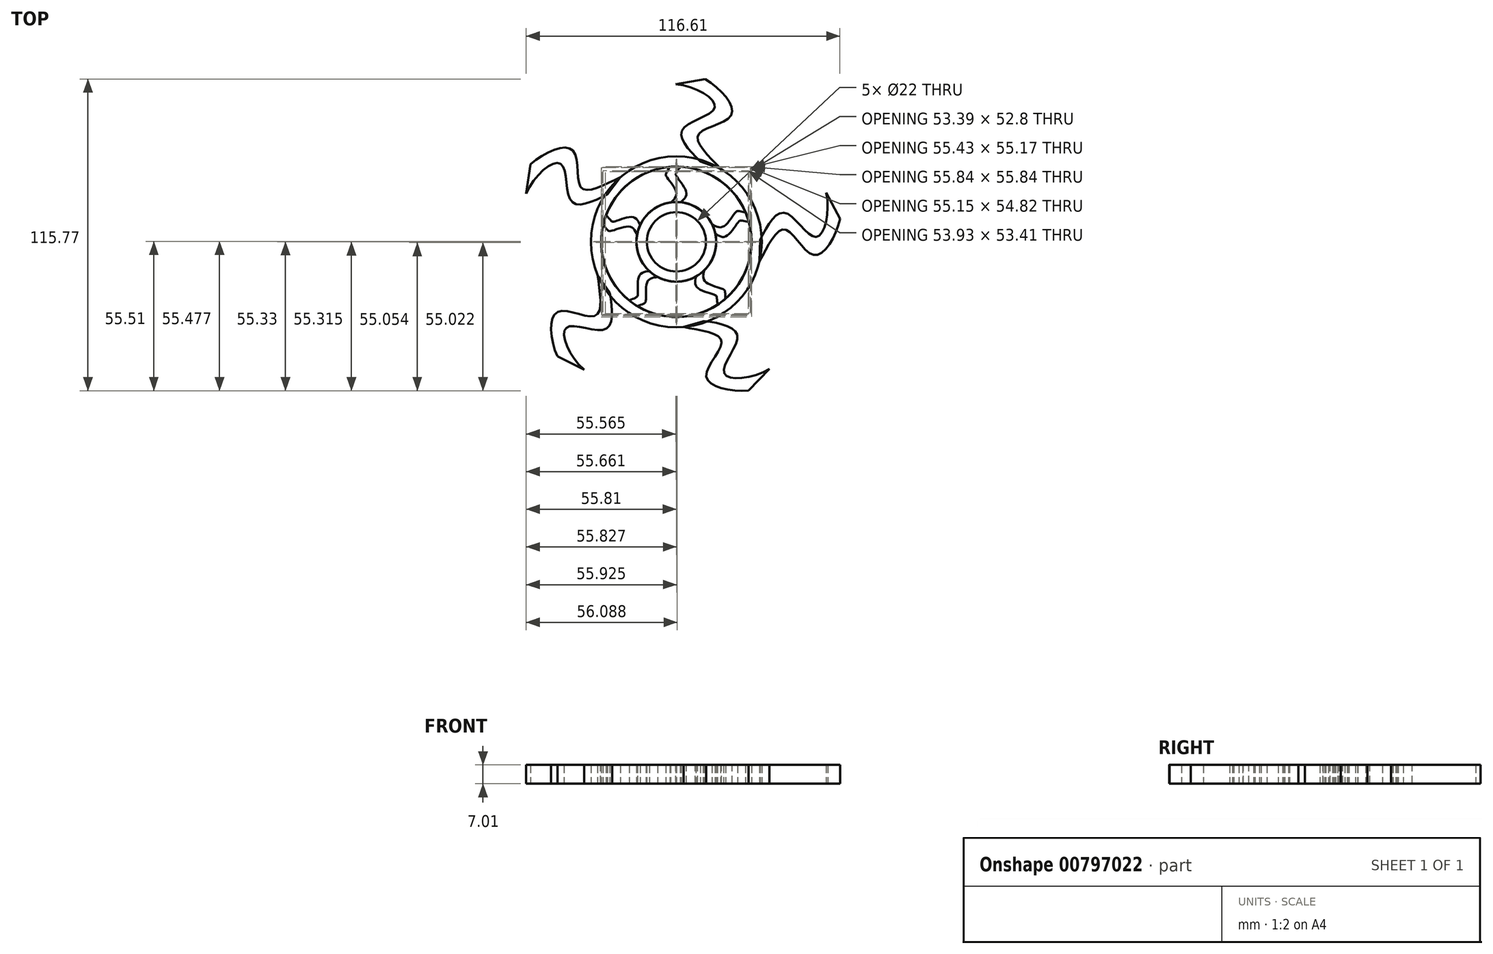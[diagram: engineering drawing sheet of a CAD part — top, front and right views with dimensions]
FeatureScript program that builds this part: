
annotation { "Feature Type Name" : "Feature", "Feature Type Description" : "" }
export const myFeature = defineFeature(function(context is Context, id is Id, definition is map)
    precondition{}
    {
        {
            var Q0;
            Q0=qCreatedBy(makeId("Top.planeOp"),FACE);
            var sketch = newSketch(context, id + "F0", { "sketchPlane" : qUnion([Q0])});
            skCircle(sketch, "E0", {"center": v(0, 0) * mm, "radius": 11 * mm});
            skCircle(sketch, "E1", {"center": v(0, 0) * mm, "radius": 31.75 * mm});
            skCircle(sketch, "E2", {"center": v(0, 0) * mm, "radius": 14.8 * mm});
            skCircle(sketch, "E3", {"center": v(0, 0) * mm, "radius": 27.94 * mm});
            skSolve(sketch);
        }
        {
            var Q0;
            Q0=makeQuery(id+"F0.imprint","IMPRINT",FACE,{"disambiguationData":[TD([[makeQuery(id+"F0.imprint","IMPRINT",EDGE,{"derivedFrom":sQuery(id+"F0.wireOp",EDGE,"E0")}),-1.0]])]});
            var Q1;
            Q1=makeQuery(id+"F0.imprint","IMPRINT",FACE,{"disambiguationData":[TD([[makeQuery(id+"F0.imprint","IMPRINT",EDGE,{"derivedFrom":sQuery(id+"F0.wireOp",EDGE,"E1")}),1.0]])]});
            extrude(context, id + "F1", {"entities" : qUnion([Q0, Q1]), "depth" : 7 * mm, "offsetDistance" : 25.4 * mm});
        }
        {
            var Q0;
            Q0=qCreatedBy(makeId("Top.planeOp"),FACE);
            var sketch = newSketch(context, id + "F2", { "sketchPlane" : qUnion([Q0])});
            skFitSpline(sketch, "E4", {"points": [v(1.35, 14.42) * mm, v(3.74, 18.24) * mm, v(0, 24.44) * mm, v(0, 25.6) * mm, v(2.24, 29.2) * mm], "startDerivative": vector(14.7, 12.34) * mm, "endDerivative": vector(10.65, 16.32) * mm});
            skFitSpline(sketch, "E5", {"points": [v(-2.38, 14.42) * mm, v(0, 18.24) * mm, v(-3.73, 24.44) * mm, v(-3.73, 25.6) * mm, v(-1.5, 29.2) * mm], "startDerivative": vector(14.7, 12.34) * mm, "endDerivative": vector(10.65, 16.32) * mm});
            skLineSegment(sketch, "E6", {"start": v(2.24, 29.2) * mm, "end": v(-1.5, 29.2) * mm});
            skLineSegment(sketch, "E7", {"start": v(1.35, 14.42) * mm, "end": v(-2.38, 14.42) * mm});
            skSolve(sketch);
        }
        {
            var Q0;
            Q0=qSketchRegion(id+"F2",true);
            var Q1;
            Q1=makeQuery(id+"F1.opExtrude","CAP_FACE",FACE,{"disambiguationData":[OSD([sQuery(id+"F0.wireOp",EDGE,"E0"),sQuery(id+"F0.wireOp",EDGE,"E2")])],"isStart":false});
            extrude(context, id + "F3", {"entities" : qUnion([Q0]), "operationType" : NewBodyOperationType.ADD, "endBound" : BoundingType.UP_TO_SURFACE, "depth" : 25.4 * mm, "endBoundEntityFace" : qUnion([Q1]), "offsetDistance" : 25.4 * mm});
        }
        {
            var Q0;
            Q0=makeQuery(id+"F3.opExtrude","SWEPT_BODY",BODY,{"disambiguationData":[OSD([sQuery(id+"F2.wireOp",EDGE,"E4"),sQuery(id+"F2.wireOp",EDGE,"E5"),sQuery(id+"F2.wireOp",EDGE,"E6"),sQuery(id+"F2.wireOp",EDGE,"E7")])]});
            var Q1;
            Q1=makeQuery(id+"F1.opExtrude","SWEPT_BODY",BODY,{"disambiguationData":[OSD([sQuery(id+"F0.wireOp",EDGE,"E0"),sQuery(id+"F0.wireOp",EDGE,"E2")])]});
            var Q2;
            Q2=makeQuery(id+"F1.opExtrude","SWEPT_FACE",FACE,{"disambiguationData":[OSD([sQuery(id+"F0.wireOp",EDGE,"E2")])]});
            circularPattern(context, id + "F4", {"entities" : qUnion([Q0, Q1]), "axis" : qUnion([Q2]), "angle" : 360 * degree, "instanceCount" : 5, "equalSpace" : true});
        }
        {
            var Q0;
            Q0=qCreatedBy(makeId("Top.planeOp"),FACE);
            var sketch = newSketch(context, id + "F5", { "sketchPlane" : qUnion([Q0])});
            skFitSpline(sketch, "E8", {"points": [v(-25.65, 17.71) * mm, v(-38.94, 15) * mm, v(-42.86, 28.89) * mm, v(-55.81, 17.9) * mm], "startDerivative": vector(-44.53, -23.57) * mm, "endDerivative": vector(-24.76, -57.77) * mm});
            skFitSpline(sketch, "E9", {"points": [v(-20.78, 24.02) * mm, v(-35.25, 20) * mm, v(-38.4, 33.9) * mm, v(-54.17, 28.89) * mm], "startDerivative": vector(-46.05, -20.37) * mm, "endDerivative": vector(-42.54, -37.45) * mm});
            skLineSegment(sketch, "E10", {"start": v(-54.17, 28.89) * mm, "end": v(-55.81, 17.9) * mm});
            skLineSegment(sketch, "E11", {"start": v(-20.78, 24.02) * mm, "end": v(-25.65, 17.71) * mm});
            skSolve(sketch);
        }
        {
            var Q0;
            Q0 = qSketchRegion(id + "F5", true);
            var Q1;
            {var subQ0=sQuery(id+"F0.wireOp",EDGE,"E2");var subQ1=sQuery(id+"F0.wireOp",EDGE,"E0");Q1=makeQuery(id+"F4.opPattern","COPY",FACE,{"derivedFrom":makeQuery(id+"F3.boolean.opBoolean","MERGE",FACE,{"derivedFrom":[makeQuery(id+"F1.opExtrude","CAP_FACE",FACE,{"disambiguationData":[OSD([subQ1,subQ0])],"isStart":false}),makeQuery(id+"F1.opExtrude","CAP_FACE",FACE,{"disambiguationData":[OSD([sQuery(id+"F0.wireOp",EDGE,"E1"),sQuery(id+"F0.wireOp",EDGE,"E3")])],"isStart":false}),makeQuery(id+"F3.opExtrude","CAP_FACE",FACE,{"disambiguationData":[OSD([subQ1,subQ0])],"isStart":false})]}),"instanceName":"3"});}
            extrude(context, id + "F6", {"entities" : qUnion([Q0]), "endBound" : BoundingType.UP_TO_SURFACE, "depth" : 25.4 * mm, "endBoundEntityFace" : qUnion([Q1]), "offsetDistance" : 25.4 * mm});
        }
        {
            var Q0;
            Q0=makeQuery(id+"F6.opExtrude","SWEPT_BODY",BODY,{"disambiguationData":[OSD([sQuery(id+"F5.wireOp",EDGE,"E8"),sQuery(id+"F5.wireOp",EDGE,"E9"),sQuery(id+"F5.wireOp",EDGE,"E10"),sQuery(id+"F5.wireOp",EDGE,"E11")])]});
            var Q1;
            Q1=sQuery(id+"F0.wireOp",EDGE,"E3");
            circularPattern(context, id + "F7", {"entities" : qUnion([Q0]), "axis" : qUnion([Q1]), "angle" : 360 * degree, "instanceCount" : 5, "equalSpace" : true});
        }
    });
